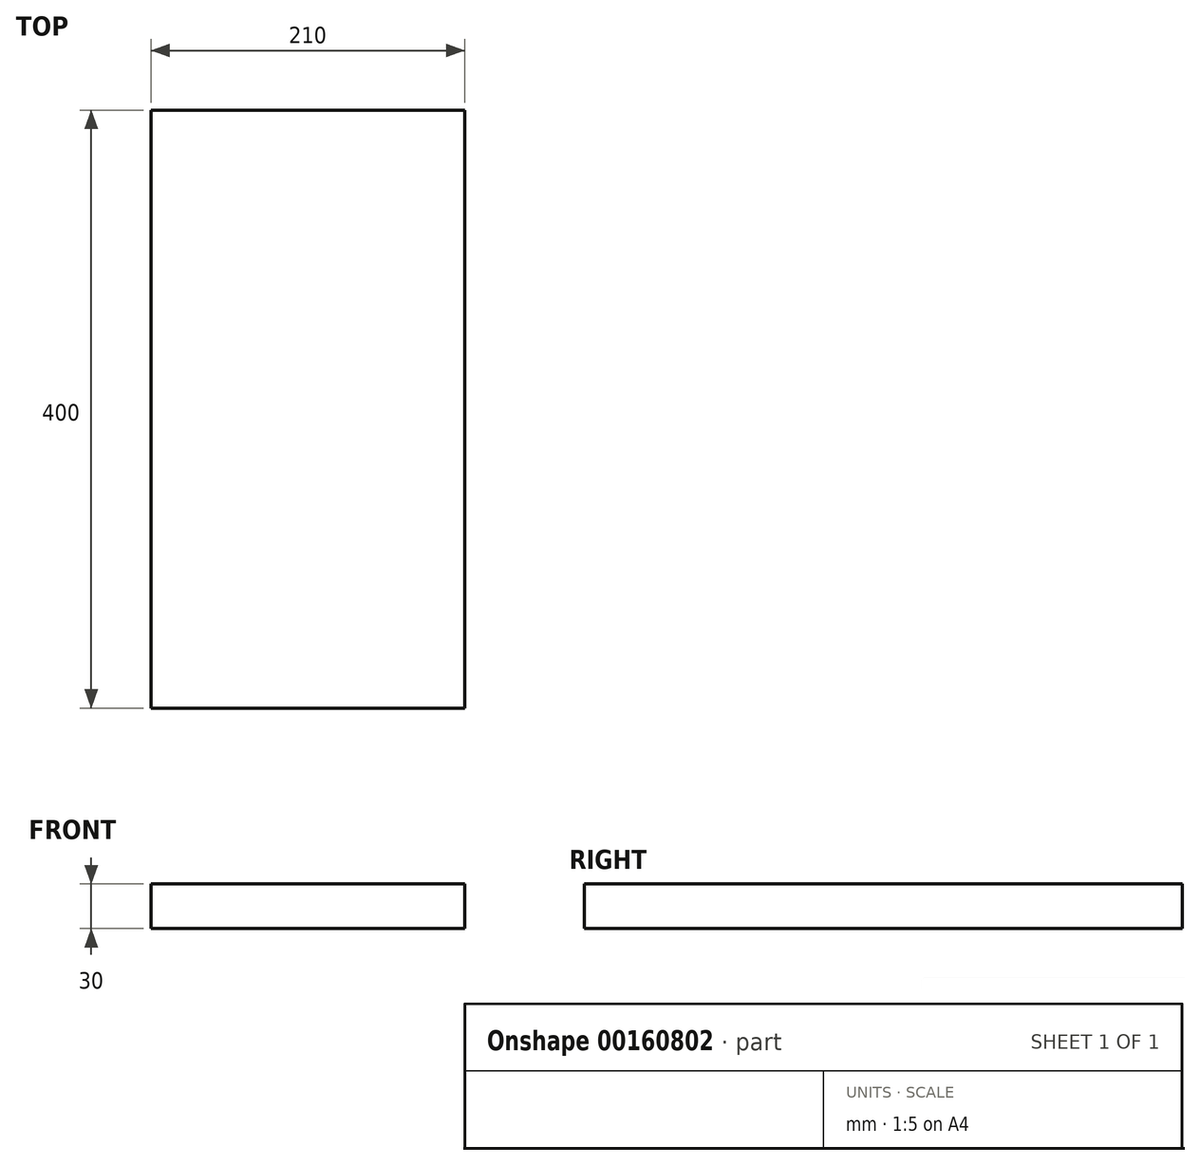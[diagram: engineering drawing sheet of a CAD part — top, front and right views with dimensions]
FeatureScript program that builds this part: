
annotation { "Feature Type Name" : "Feature", "Feature Type Description" : "" }
export const myFeature = defineFeature(function(context is Context, id is Id, definition is map)
    precondition{}
    {
        {
            var Q0;
            Q0=qCreatedBy(makeId("Front.planeOp"),FACE);
            var sketch = newSketch(context, id + "F0", { "sketchPlane" : qUnion([Q0])});
            skLineSegment(sketch, "E0.bottom", {"start": v(-111.17, 30) * mm, "end": v(98.83, 30) * mm});
            skLineSegment(sketch, "E0.top", {"start": v(-111.17, 0) * mm, "end": v(98.83, 0) * mm});
            skLineSegment(sketch, "E0.left", {"start": v(-111.17, 30) * mm, "end": v(-111.17, 0) * mm});
            skLineSegment(sketch, "E0.right", {"start": v(98.83, 30) * mm, "end": v(98.83, 0) * mm});
            skSolve(sketch);
        }
        {
            var Q0;
            Q0=makeQuery(id+"F0.imprint","IMPRINT",FACE,{"disambiguationData":[TD([[makeQuery(id+"F0.imprint","IMPRINT",EDGE,{"derivedFrom":sQuery(id+"F0.wireOp",EDGE,"E0.bottom")}),-1.0]])]});
            extrude(context, id + "F1", {"entities" : qUnion([Q0]), "depth" : 400 * mm});
        }
    });
